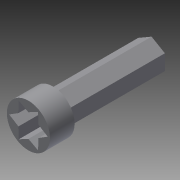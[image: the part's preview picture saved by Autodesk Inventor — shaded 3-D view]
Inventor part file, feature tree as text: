
AUTODESK INVENTOR PART (.ipt)
format: ipt  version: 2015 (Build 190159000, 159)  size: 125,952 bytes
history: native  units: in
note: dims shown in document units (in); Inventor stores cm internally (conversion verified against a paired STEP export)
features: extrude x4, sketch x4, projected_geometry x1
ambient origin geometry x8: Origin, YZ Plane, XZ Plane, XY Plane, X Axis, Y Axis, Z Axis, Center Point
bodies: Solid1 (feature_tree)
feature tree (9):
  extrude  "Extrusion1"  Depth=0.1083in
  extrude  "Extrusion2"  Depth=1.0in
  extrude  "Extrusion3"  Depth=0.2in
  extrude  "Extrusion4"  Depth=0.175in
  sketch  "Sketch1"  dims[d0=0.25in d1=0.1083in]
  sketch  "Sketch2"  dims[d2=1.0in d3=0.0in d4=0.35in]
  sketch  "Sketch3"  dims[d5=0.2in d6=0.0in d7=0.313in]
  sketch  "Sketch4"  dims[d8=0.1875in d9=0.0796in d10=60.0deg d11=0.0938in d12=2.3622in d14=360.0deg d16=0.175in d17=0.0in d18=0.175in d19=0.0in]
  projected_geometry  "Projected Loop1"
